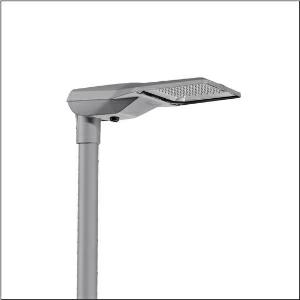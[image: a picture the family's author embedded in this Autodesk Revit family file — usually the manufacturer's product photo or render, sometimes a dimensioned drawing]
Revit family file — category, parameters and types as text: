
# Revit family: streetlight_sl_21_midi___st1_0a_5xe3d33r08nb_ea4c
name_source: partatom
category: Lighting Fixtures
units: mm (PartAtom-declared; Revit-internal decimal feet)

## family parameters
Cut with Voids When Loaded = No
Host = Face
Light Source = No
Part Type = Normal
Room Calculation Point = No
Round Connector Dimension = Use Diameter
Shared = No

## types (1)
- --- (1 x LED, 22700 lm, 151.2 W, 3000K)
    Apparent Load = 151 VA
    CIE Flux Codes = 40 73 97 100 100
    Color Rendering = 70
    Color Temperature = 3000K
    Default Elevation = 1800 mm
    Description = Streetlight SL 21 midi, mast luminaire, primary light control with lens, of PMMA, primary optical cover: cover, of toughened safety glass, transparent, light distribution: ST1.0a, light emission: direct distribution, primary light characteristic: asymmetric, installation type: side-entry, post-top, LED, High Power LED, rated luminous flux: 22.700lm, luminous efficacy: 150lm/W, light colour: 730, colour temperature: 3000K, control: flexible luminous flux parameterisation, time-dependent luminous flux control, constant luminous flux control, overheat protection, presetting dimming logarithmic, mains connection: 230..240V, AC, 50/60Hz, start of lifetime: 151W, end of service life: 157W, reduction: 70W, luminaire housing, of diecast aluminium, powder-coated, Siteco® metallic grey (DB 702S), corrosivity category C5 mid according to DIN EN ISO 12944, please order mast flange separately, inclination adjustable: 0°, 5°, 10°, 15°, sealing non-destructively replaceable, multi-level sealing system, length: 644mm, width: 335mm, height: 110mm, mast flange for spigot size: 42mm (side-entry): 5XC10008XM4, 60/48mm (side-entry/post-top): 5XC10108XM2, 76/60mm (side-entry/post-top): 5XC10108XM1, Smart Interface below, protection rating (complete): IP66, insulation class (complete): insulation class II (safety insulation), certification: CE, ENEC, ENEC+, VDE, impact resistance: IK09, permissible operating ambient temperature for outdoor applications: -40..+50°C, standard-compliant lighting for roads and squares, packaging unit: 1 piece

Light Distribution: ST1.0a
    Height = 111 mm
    Lamp = 1 x LED
    Lamp Light Flux = 22700 lm
    Lamp Power = 151.2 W
    Lamp count = 1
    Length = 644 mm
    Luminous efficacy = 150 lm/W
    Manufacturer = Siteco
    ModVariant = No
    Model = 5XE3D33R08NB
    Number of Poles = 1
    OnlyDefault = Yes
    Power Factor = 1
    Product Name = Streetlight SL 21 midi | ST1.0a
    Product group = mast luminaire | pylon top
    ProductGroupID = 6100
    Protection Class = Protection class II
    Protection Degree = IP 66
    RLX_Detail_Level = 1
    RLX_Emergency_Light_Flux = 0 lm
    RLX_Emergency_Type = 0
    RLX_Emergency_Type_DB = No
    RlxData = <blob elided: 91233 chars, md5=8feebb8a>
    Socket = socket
    Standby Power = 0 W
    System Light Flux = 22700 lm
    System Power = 151 W
    Type Comments = factory setting: luminous flux: 100 % | dim-lin: 254 | 802 mA
    Type Image = l_1004300.jpg
    URL = http://relux.com
    VarID = @adj_121237
    Voltage = 0 V
    Weight = 0.00 kg
    Width = 336 mm

## geometry (parser evidence)
native form markers: Blend x4, Sweep x10
no freeform markers — native parametric forms only
